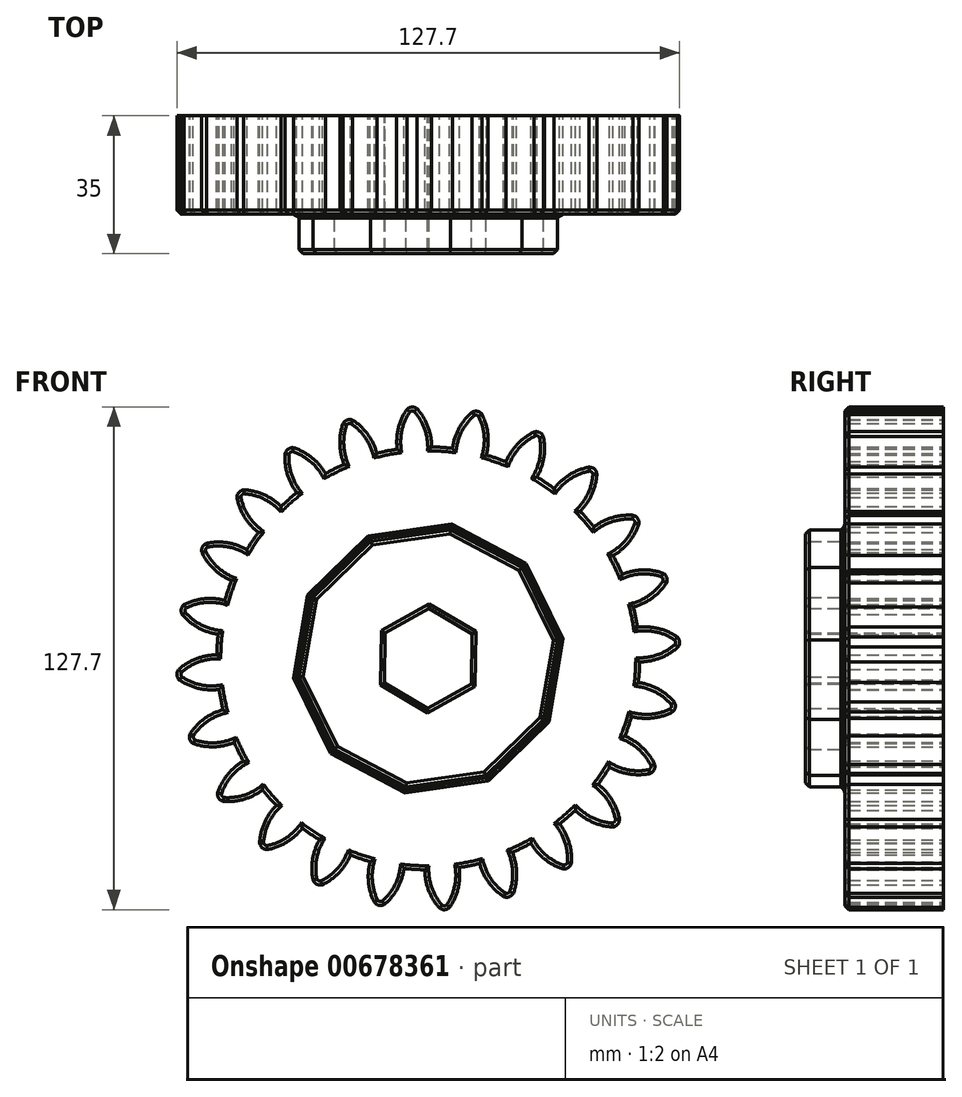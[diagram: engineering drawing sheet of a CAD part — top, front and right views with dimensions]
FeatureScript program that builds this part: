
annotation { "Feature Type Name" : "Feature", "Feature Type Description" : "" }
export const myFeature = defineFeature(function(context is Context, id is Id, definition is map)
    precondition{}
    {
        {
            var Q0;
            Q0=qCreatedBy(makeId("Front.planeOp"),FACE);
            var sketch = newSketch(context, id + "F0", { "sketchPlane" : qUnion([Q0])});
            skCircle(sketch, "E0", {"center": v(0, 0) * mm, "radius": 53.72 * mm});
            skCircle(sketch, "E1", {"center": v(0, 0) * mm, "radius": 58.67 * mm, "construction": true});
            skCircle(sketch, "E2", {"center": v(0, 0) * mm, "radius": 63.5 * mm, "construction": true});
            skLineSegment(sketch, "E3", {"start": v(0, 0) * mm, "end": v(0, 78.03) * mm, "construction": true});
            skLineSegment(sketch, "E4", {"start": v(0, 0) * mm, "end": v(-5.6, 85.42) * mm, "construction": true});
            skLineSegment(sketch, "E5", {"start": v(0, 58.67) * mm, "end": v(-59.1, 58.67) * mm, "construction": true});
            skLineSegment(sketch, "E6", {"start": v(0, 58.67) * mm, "end": v(-58.88, 37.24) * mm, "construction": true});
            skCircle(sketch, "E7", {"center": v(0, 0) * mm, "radius": 55.14 * mm, "construction": true});
            skCircle(sketch, "E8", {"center": v(0, 58.67) * mm, "radius": 14.6 * mm, "construction": true});
            skCircle(sketch, "E9", {"center": v(-13.72, 53.68) * mm, "radius": 14.6 * mm, "construction": true});
            skArc(sketch, "E10", {"start": v(0, 58.67) * mm, "mid": v(-1.2, 61.2) * mm, "end": v(-2.86, 63.44) * mm});
            skArc(sketch, "E11", {"start": v(0.88, 53.71) * mm, "mid": v(0.65, 56.23) * mm, "end": v(0, 58.67) * mm});
            skArc(sketch, "E12.MirrorCS", {"start": v(-7.66, 58.17) * mm, "mid": v(-6.8, 60.83) * mm, "end": v(-5.45, 63.27) * mm});
            skArc(sketch, "E13.MirrorCS", {"start": v(-7.88, 53.14) * mm, "mid": v(-7.99, 55.67) * mm, "end": v(-7.66, 58.17) * mm});
            skArc(sketch, "E14", {"start": v(-2.86, 63.44) * mm, "mid": v(-4.18, 63.85) * mm, "end": v(-5.45, 63.27) * mm});
            skCircle(sketch, "E15.cCircle", {"center": v(0, 0) * mm, "radius": 31.52 * mm, "construction": true});
            skLineSegment(sketch, "E15.0", {"start": v(-5.65, -32.65) * mm, "end": v(-23.76, -23.1) * mm});
            skLineSegment(sketch, "E15.1", {"start": v(-23.76, -23.1) * mm, "end": v(-32.8, -4.72) * mm});
            skLineSegment(sketch, "E15.2", {"start": v(-32.8, -4.72) * mm, "end": v(-29.31, 15.46) * mm});
            skLineSegment(sketch, "E15.3", {"start": v(-29.31, 15.46) * mm, "end": v(-14.63, 29.74) * mm});
            skLineSegment(sketch, "E15.4", {"start": v(-14.63, 29.74) * mm, "end": v(5.65, 32.65) * mm});
            skLineSegment(sketch, "E15.5", {"start": v(5.65, 32.65) * mm, "end": v(23.76, 23.1) * mm});
            skLineSegment(sketch, "E15.6", {"start": v(23.76, 23.1) * mm, "end": v(32.8, 4.72) * mm});
            skLineSegment(sketch, "E15.7", {"start": v(32.8, 4.72) * mm, "end": v(29.31, -15.46) * mm});
            skLineSegment(sketch, "E15.8", {"start": v(29.31, -15.46) * mm, "end": v(14.63, -29.74) * mm});
            skLineSegment(sketch, "E15.9", {"start": v(14.63, -29.74) * mm, "end": v(-5.65, -32.65) * mm});
            skPoint(sketch, "E15.0.midPoint", {"position": v(-14.7, -27.88) * mm});
            skCircle(sketch, "E16.cCircle", {"center": v(0, 0) * mm, "radius": 11.02 * mm, "construction": true});
            skLineSegment(sketch, "E16.0", {"start": v(-0.15, -12.72) * mm, "end": v(-11.1, -6.23) * mm});
            skLineSegment(sketch, "E16.1", {"start": v(-11.1, -6.23) * mm, "end": v(-10.94, 6.5) * mm});
            skLineSegment(sketch, "E16.2", {"start": v(-10.94, 6.5) * mm, "end": v(0.15, 12.72) * mm});
            skLineSegment(sketch, "E16.3", {"start": v(0.15, 12.72) * mm, "end": v(11.1, 6.23) * mm});
            skLineSegment(sketch, "E16.4", {"start": v(11.1, 6.23) * mm, "end": v(10.94, -6.5) * mm});
            skLineSegment(sketch, "E16.5", {"start": v(10.94, -6.5) * mm, "end": v(-0.15, -12.72) * mm});
            skPoint(sketch, "E16.0.midPoint", {"position": v(-5.62, -9.48) * mm});
            skSolve(sketch);
        }
        {
            var Q0;
            {var subQ0=sQuery(id+"F0.wireOp",EDGE,"E0");var subQ1=makeQuery(id+"F0.imprint","INTERSECT",VERTEX,{"derivedFrom":[subQ0,sQuery(id+"F0.wireOp",EDGE,"E11")]});Q0=makeQuery(id+"F0.imprint","IMPRINT",FACE,{"disambiguationData":[TD([[makeQuery(id+"F0.imprint","IMPRINT",EDGE,{"disambiguationData":[TD([[subQ1,-1.0]])],"derivedFrom":subQ0}),1.0]])]});}
            var Q1;
            Q1=makeQuery(id+"F0.imprint","IMPRINT",FACE,{"disambiguationData":[TD([[makeQuery(id+"F0.imprint","IMPRINT",EDGE,{"derivedFrom":sQuery(id+"F0.wireOp",EDGE,"E10")}),1.0]])]});
            extrude(context, id + "F1", {"entities" : qUnion([Q0, Q1]), "depth" : 25 * mm, "offsetDistance" : 25 * mm});
        }
        {
            var Q0;
            Q0=makeQuery(id+"F1.opExtrude","SWEPT_BODY",BODY,{"disambiguationData":[OSD([sQuery(id+"F0.wireOp",EDGE,"E0"),sQuery(id+"F0.wireOp",EDGE,"E10"),sQuery(id+"F0.wireOp",EDGE,"E11"),sQuery(id+"F0.wireOp",EDGE,"E12.MirrorCS"),sQuery(id+"F0.wireOp",EDGE,"E13.MirrorCS"),sQuery(id+"F0.wireOp",EDGE,"E14")])]});
            var Q1;
            Q1=makeQuery(id+"F1.opExtrude","SWEPT_FACE",FACE,{"disambiguationData":[OSD([sQuery(id+"F0.wireOp",EDGE,"E0")])]});
            circularPattern(context, id + "F2", {"entities" : qUnion([Q0]), "axis" : qUnion([Q1]), "angle" : 360 * degree, "instanceCount" : 24, "equalSpace" : true});
        }
        {
            var Q0;
            Q0=makeQuery(id+"F0.imprint","IMPRINT",FACE,{"disambiguationData":[TD([[makeQuery(id+"F0.imprint","IMPRINT",EDGE,{"derivedFrom":sQuery(id+"F0.wireOp",EDGE,"E15.0")}),-1.0]])]});
            extrude(context, id + "F3", {"entities" : qUnion([Q0]), "operationType" : NewBodyOperationType.ADD, "depth" : 35 * mm, "offsetDistance" : 25 * mm});
        }
        {
            var Q0;
            {var subQ0=makeQuery(id+"F1.opExtrude","CAP_FACE",FACE,{"disambiguationData":[OSD([sQuery(id+"F0.wireOp",EDGE,"E0"),sQuery(id+"F0.wireOp",EDGE,"E10"),sQuery(id+"F0.wireOp",EDGE,"E11"),sQuery(id+"F0.wireOp",EDGE,"E12.MirrorCS"),sQuery(id+"F0.wireOp",EDGE,"E13.MirrorCS"),sQuery(id+"F0.wireOp",EDGE,"E14"),sQuery(id+"F0.wireOp",EDGE,"E15.0"),sQuery(id+"F0.wireOp",EDGE,"E15.1"),sQuery(id+"F0.wireOp",EDGE,"E15.2"),sQuery(id+"F0.wireOp",EDGE,"E15.3"),sQuery(id+"F0.wireOp",EDGE,"E15.4"),sQuery(id+"F0.wireOp",EDGE,"E15.5"),sQuery(id+"F0.wireOp",EDGE,"E15.6"),sQuery(id+"F0.wireOp",EDGE,"E15.7"),sQuery(id+"F0.wireOp",EDGE,"E15.8"),sQuery(id+"F0.wireOp",EDGE,"E15.9")])],"isStart":false});Q0=makeQuery(id+"F3.boolean.opBoolean","MERGE",FACE,{"derivedFrom":[subQ0,makeQuery(id+"F2.opPattern","COPY",FACE,{"derivedFrom":subQ0,"instanceName":"1"}),makeQuery(id+"F2.opPattern","COPY",FACE,{"derivedFrom":subQ0,"instanceName":"2"}),makeQuery(id+"F2.opPattern","COPY",FACE,{"derivedFrom":subQ0,"instanceName":"3"}),makeQuery(id+"F2.opPattern","COPY",FACE,{"derivedFrom":subQ0,"instanceName":"4"}),makeQuery(id+"F2.opPattern","COPY",FACE,{"derivedFrom":subQ0,"instanceName":"5"}),makeQuery(id+"F2.opPattern","COPY",FACE,{"derivedFrom":subQ0,"instanceName":"6"}),makeQuery(id+"F2.opPattern","COPY",FACE,{"derivedFrom":subQ0,"instanceName":"7"}),makeQuery(id+"F2.opPattern","COPY",FACE,{"derivedFrom":subQ0,"instanceName":"8"}),makeQuery(id+"F2.opPattern","COPY",FACE,{"derivedFrom":subQ0,"instanceName":"9"}),makeQuery(id+"F2.opPattern","COPY",FACE,{"derivedFrom":subQ0,"instanceName":"10"}),makeQuery(id+"F2.opPattern","COPY",FACE,{"derivedFrom":subQ0,"instanceName":"11"}),makeQuery(id+"F2.opPattern","COPY",FACE,{"derivedFrom":subQ0,"instanceName":"12"}),makeQuery(id+"F2.opPattern","COPY",FACE,{"derivedFrom":subQ0,"instanceName":"13"}),makeQuery(id+"F2.opPattern","COPY",FACE,{"derivedFrom":subQ0,"instanceName":"14"}),makeQuery(id+"F2.opPattern","COPY",FACE,{"derivedFrom":subQ0,"instanceName":"15"}),makeQuery(id+"F2.opPattern","COPY",FACE,{"derivedFrom":subQ0,"instanceName":"16"}),makeQuery(id+"F2.opPattern","COPY",FACE,{"derivedFrom":subQ0,"instanceName":"17"}),makeQuery(id+"F2.opPattern","COPY",FACE,{"derivedFrom":subQ0,"instanceName":"18"}),makeQuery(id+"F2.opPattern","COPY",FACE,{"derivedFrom":subQ0,"instanceName":"19"}),makeQuery(id+"F2.opPattern","COPY",FACE,{"derivedFrom":subQ0,"instanceName":"20"}),makeQuery(id+"F2.opPattern","COPY",FACE,{"derivedFrom":subQ0,"instanceName":"21"}),makeQuery(id+"F2.opPattern","COPY",FACE,{"derivedFrom":subQ0,"instanceName":"22"}),makeQuery(id+"F2.opPattern","COPY",FACE,{"derivedFrom":subQ0,"instanceName":"23"})]});}
            var Q1;
            Q1=makeQuery(id+"F3.opExtrude","CAP_FACE",FACE,{"disambiguationData":[OSD([sQuery(id+"F0.wireOp",EDGE,"E15.0"),sQuery(id+"F0.wireOp",EDGE,"E15.1"),sQuery(id+"F0.wireOp",EDGE,"E15.2"),sQuery(id+"F0.wireOp",EDGE,"E15.3"),sQuery(id+"F0.wireOp",EDGE,"E15.4"),sQuery(id+"F0.wireOp",EDGE,"E15.5"),sQuery(id+"F0.wireOp",EDGE,"E15.6"),sQuery(id+"F0.wireOp",EDGE,"E15.7"),sQuery(id+"F0.wireOp",EDGE,"E15.8"),sQuery(id+"F0.wireOp",EDGE,"E15.9"),sQuery(id+"F0.wireOp",EDGE,"E16.0"),sQuery(id+"F0.wireOp",EDGE,"E16.1"),sQuery(id+"F0.wireOp",EDGE,"E16.2"),sQuery(id+"F0.wireOp",EDGE,"E16.3"),sQuery(id+"F0.wireOp",EDGE,"E16.4"),sQuery(id+"F0.wireOp",EDGE,"E16.5")])],"isStart":false});
            chamfer(context, id + "F4", {"entities" : qUnion([Q0, Q1]), "width" : 1 * mm, "tangentPropagation" : true});
        }
    });
